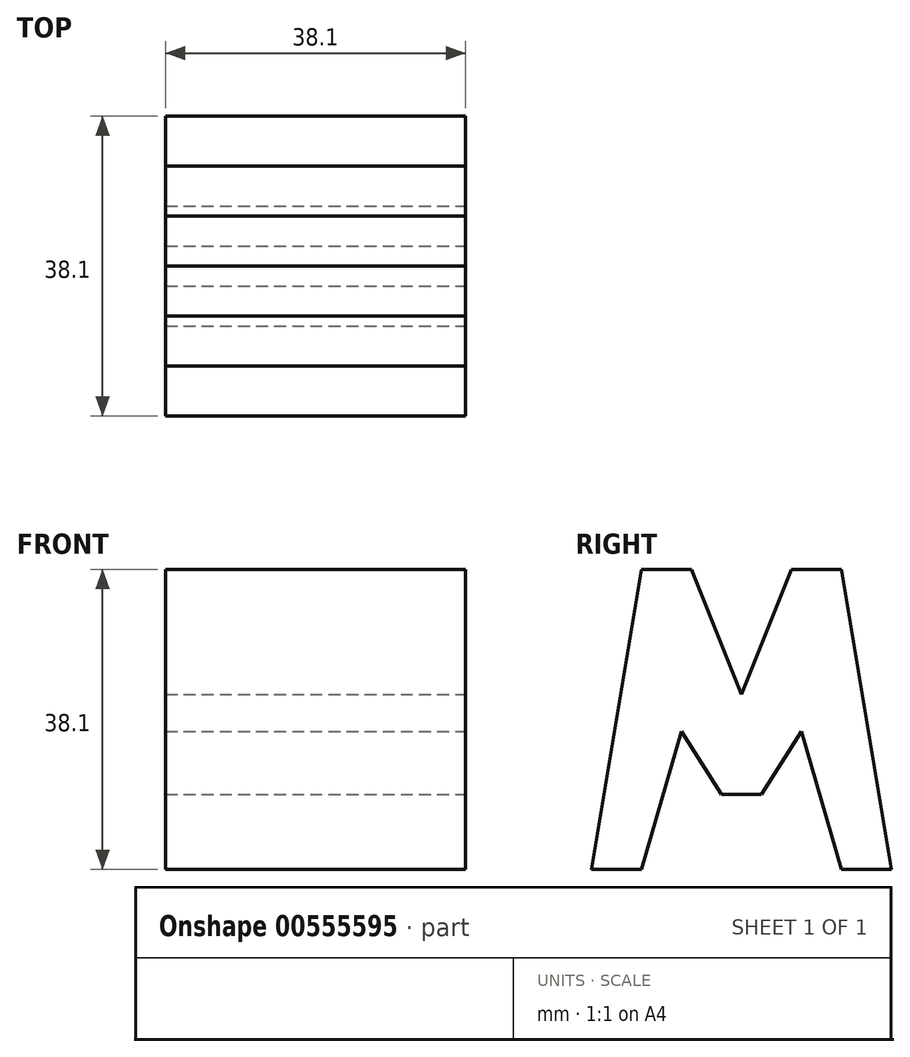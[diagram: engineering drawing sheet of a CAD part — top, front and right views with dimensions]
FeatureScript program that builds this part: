
annotation { "Feature Type Name" : "Feature", "Feature Type Description" : "" }
export const myFeature = defineFeature(function(context is Context, id is Id, definition is map)
    precondition{}
    {
        {
            var Q0;
            Q0=qCreatedBy(makeId("Front.planeOp"),FACE);
            var sketch = newSketch(context, id + "F0", { "sketchPlane" : qUnion([Q0])});
            skLineSegment(sketch, "E0", {"start": v(0, 0) * mm, "end": v(0, 38.1) * mm});
            skLineSegment(sketch, "E1", {"start": v(0, 0) * mm, "end": v(38.1, 0) * mm});
            skLineSegment(sketch, "E2", {"start": v(38.1, 0) * mm, "end": v(38.1, 38.1) * mm});
            skLineSegment(sketch, "E3", {"start": v(0, 38.1) * mm, "end": v(38.1, 38.1) * mm});
            skSolve(sketch);
        }
        {
            var Q0;
            Q0 = qSketchRegion(id + "F0", true);
            extrude(context, id + "F1", {"entities" : qUnion([Q0]), "depth" : 38.1 * mm, "offsetDistance" : 25.4 * mm});
        }
        {
            var Q0;
            Q0=qCreatedBy(makeId("Front.planeOp"),FACE);
            cPlane(context, id + "F2", {"entities" : qUnion([Q0]), "cplaneType" : CPlaneType.OFFSET, "offset" : 38.1 * mm, "width" : 152.4 * mm, "height" : 152.4 * mm});
        }
        {
            var Q0;
            Q0=qCreatedBy(makeId("Right.planeOp"),FACE);
            var Q1;
            Q1 = qBodyType(qCreatedBy(id + "F4" ,EDGE), BodyType.WIRE);
            cPlane(context, id + "F3", {"entities" : qUnion([Q0, Q1]), "cplaneType" : CPlaneType.OFFSET, "offset" : 38.1 * mm, "width" : 152.4 * mm, "height" : 152.4 * mm});
        }
        {
            var Q0;
            Q0=qCreatedBy(id+"F3.planeOp",FACE);
            var sketch = newSketch(context, id + "F4", { "sketchPlane" : qUnion([Q0])});
            skSolve(sketch);
        }
        {
            var Q0;
            Q0=makeQuery(id+"F1.opExtrude","SWEPT_FACE",FACE,{"disambiguationData":[OSD([sQuery(id+"F0.wireOp",EDGE,"E2")])]});
            var sketch = newSketch(context, id + "F5", { "sketchPlane" : qUnion([Q0])});
            skLineSegment(sketch, "E4", {"start": v(-38.1, 38.1) * mm, "end": v(-38.1, 0) * mm});
            skLineSegment(sketch, "E5", {"start": v(-38.1, 0) * mm, "end": v(-31.75, 38.1) * mm});
            skLineSegment(sketch, "E6", {"start": v(-31.75, 38.1) * mm, "end": v(-25.4, 38.1) * mm});
            skLineSegment(sketch, "E7", {"start": v(-19.05, 22.23) * mm, "end": v(-12.7, 38.1) * mm});
            skLineSegment(sketch, "E8", {"start": v(-12.7, 38.1) * mm, "end": v(-6.35, 38.1) * mm});
            skLineSegment(sketch, "E9", {"start": v(-6.35, 38.1) * mm, "end": v(0, 0) * mm});
            skLineSegment(sketch, "E10", {"start": v(-38.1, 0) * mm, "end": v(-31.75, 0) * mm});
            skLineSegment(sketch, "E11", {"start": v(-31.75, 0) * mm, "end": v(-26.67, 17.55) * mm});
            skLineSegment(sketch, "E12", {"start": v(-26.67, 17.55) * mm, "end": v(-21.6, 9.52) * mm});
            skLineSegment(sketch, "E13", {"start": v(-21.6, 9.53) * mm, "end": v(-16.51, 9.53) * mm});
            skLineSegment(sketch, "E14", {"start": v(-16.51, 9.53) * mm, "end": v(-11.43, 17.55) * mm});
            skLineSegment(sketch, "E15", {"start": v(-11.43, 17.55) * mm, "end": v(-6.35, 0) * mm});
            skLineSegment(sketch, "E16", {"start": v(-6.35, 0) * mm, "end": v(0, 0) * mm});
            skLineSegment(sketch, "E17", {"start": v(-25.4, 38.1) * mm, "end": v(-19.05, 22.23) * mm});
            skSolve(sketch);
        }
        {
            var Q0;
            {var subQ0=sQuery(id+"F5.wireOp",EDGE,"E4");Q0=makeQuery(id+"F5.imprint","IMPRINT",FACE,{"disambiguationData":[TD([[makeQuery(id+"F5.imprint","IMPRINT",EDGE,{"derivedFrom":subQ0}),-1.0]])]});}
            var Q1;
            {var subQ0=sQuery(id+"F5.wireOp",EDGE,"E7");Q1=makeQuery(id+"F5.imprint","IMPRINT",FACE,{"disambiguationData":[TD([[makeQuery(id+"F5.imprint","IMPRINT",EDGE,{"derivedFrom":subQ0}),1.0]])]});}
            var Q2;
            {var subQ0=sQuery(id+"F5.wireOp",EDGE,"E9");Q2=makeQuery(id+"F5.imprint","IMPRINT",FACE,{"disambiguationData":[TD([[makeQuery(id+"F5.imprint","IMPRINT",EDGE,{"derivedFrom":subQ0}),1.0]])]});}
            var Q3;
            {var subQ0=sQuery(id+"F5.wireOp",EDGE,"E11");Q3=makeQuery(id+"F5.imprint","IMPRINT",FACE,{"disambiguationData":[TD([[makeQuery(id+"F5.imprint","IMPRINT",EDGE,{"derivedFrom":subQ0}),-1.0]])]});}
            extrude(context, id + "F6", {"entities" : qUnion([Q0, Q1, Q2, Q3]), "operationType" : NewBodyOperationType.REMOVE, "oppositeDirection" : true, "depth" : 38.1 * mm, "offsetDistance" : 25.4 * mm});
        }
    });
